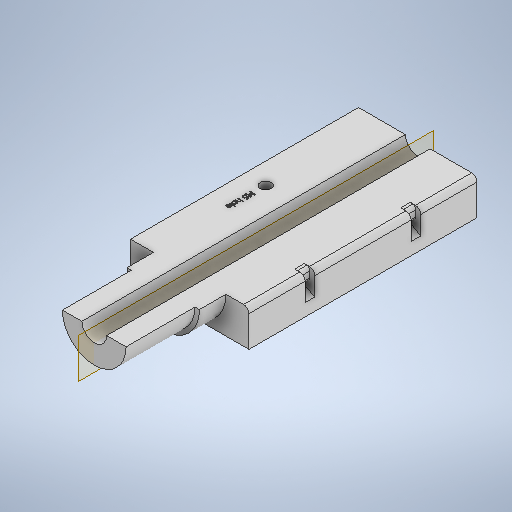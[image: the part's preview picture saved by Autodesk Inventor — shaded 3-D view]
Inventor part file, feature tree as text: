
AUTODESK INVENTOR PART (.ipt)
format: ipt  version: 2025 (Build 290162000, 162)  size: 745,984 bytes
history: native  units: mm
features: sketch x11, extrude x5, hole x4, emboss x2, plane x1, mirror x1, fillet x1
ambient origin geometry x8: Origin, YZ Plane, XZ Plane, XY Plane, X Axis, Y Axis, Z Axis, Center Point
bodies: Solid1 (feature_tree)
feature tree (25):
  extrude  "Extrusion1"  Depth=129.0mm
  extrude  "Extrusion2"  Depth=20.5mm
  extrude  "Extrusion3"  Depth=15.0mm TaperAngle=0.0deg
  extrude  "Extrusion4"  TaperAngle=180.0deg  [1 undecoded]
  plane  "Work Plane1"
  extrude  "Extrusion5"  Depth=7.0mm
  mirror  "Mirror1"
  fillet  "Fillet1"  [1 undecoded]
  hole  "Hole1"  [1 undecoded]
  emboss  "Emboss1"
  hole  "Hole2"  [1 undecoded]
  hole  "Hole3"  [1 undecoded]
  hole  "Hole4"  [1 undecoded]
  emboss  "Emboss2"
  sketch  "Sketch1"  dims[d0=20.5mm d1=129.0mm]
  sketch  "Sketch2"  dims[d2=67.0mm d3=0.0mm d4=20.5mm]
  sketch  "Sketch3"  dims[d5=180.0deg d6=15.0mm d7=0.0mm]
  sketch  "Sketch4"  dims[d8=18.0mm d9=180.0deg]
  sketch  "Sketch5"  dims[d10=39.0mm d11=0.0mm d12=7.0mm d13=180.0deg]
  sketch  "Sketch6"  dims[d14=0.0mm d15=0.0mm d16=30.0mm]
  sketch  "Sketch7"  dims[d17=2.0mm d18=1.5mm d19=1.0mm d20=5.4mm d21=0.0mm]
  sketch  "Sketch9"  dims[d22=3.0mm]
  sketch  "Sketch10"  dims[d23=6.2mm d24=6.0mm d25=10.5mm d26=6.0mm d27=90.0deg d28=10.0mm d29=0.0mm d30=12.0mm]
  sketch  "Sketch11"  dims[d31=1.0mm d32=0.0mm]
  sketch  "Sketch12"  dims[d33=5.2mm d34=6.0mm d35=4.0mm d36=2.0mm d37=90.0deg d38=10.0mm d39=0.0mm d40=5.2mm d41=6.0mm d42=4.0mm d43=2.0mm d44=90.0deg d45=10.0mm d46=0.0mm d47=6.55mm d48=6.0mm d49=4.0mm d50=2.0mm d51=90.0deg d52=10.0mm d53=0.0mm d54=152.0mm d55=67.0mm d56=110.0mm d57=1.0mm d58=0.0mm]
note: 6 required parameter values undecoded (feature->parameter linkage not recoverable at this tier; creation-order binding heuristic only, values carry confidence <= 0.55)
